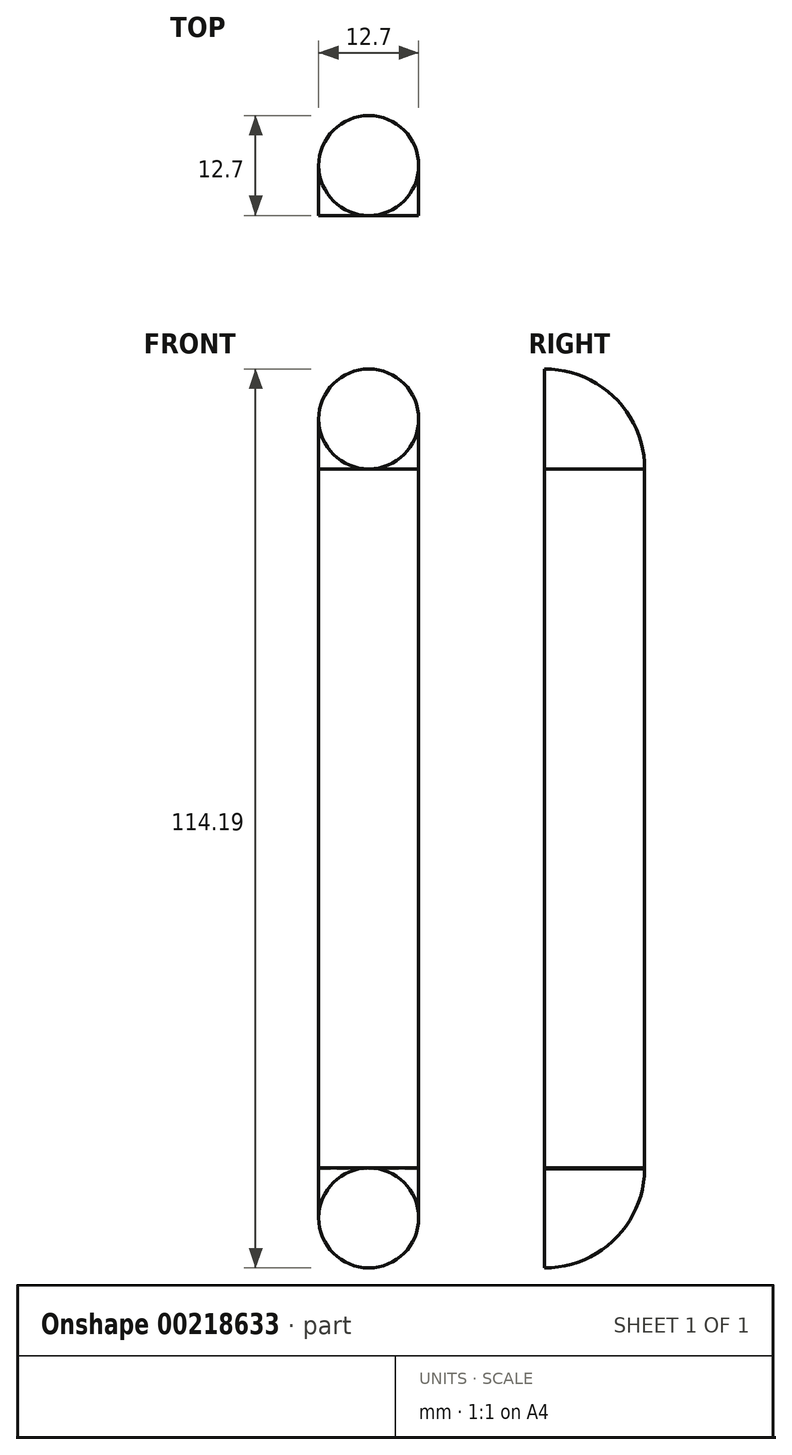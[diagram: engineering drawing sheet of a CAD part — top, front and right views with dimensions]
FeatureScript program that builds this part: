
annotation { "Feature Type Name" : "Feature", "Feature Type Description" : "" }
export const myFeature = defineFeature(function(context is Context, id is Id, definition is map)
    precondition{}
    {
        {
            var Q0;
            Q0=qCreatedBy(makeId("Front.planeOp"),FACE);
            var sketch = newSketch(context, id + "F0", { "sketchPlane" : qUnion([Q0])});
            skCircle(sketch, "E0", {"center": v(0, 53.81) * mm, "radius": 6.35 * mm});
            skCircle(sketch, "E1", {"center": v(0, -47.68) * mm, "radius": 6.35 * mm});
            skLineSegment(sketch, "E2", {"start": v(0, 47.46) * mm, "end": v(51.11, 47.46) * mm});
            skLineSegment(sketch, "E3", {"start": v(0, 47.46) * mm, "end": v(-41.36, 47.46) * mm});
            skLineSegment(sketch, "E4", {"start": v(0, -41.33) * mm, "end": v(50.82, -41.33) * mm});
            skLineSegment(sketch, "E5", {"start": v(0, -41.33) * mm, "end": v(-37.52, -41.33) * mm});
            skSolve(sketch);
        }
        {
            var Q0;
            Q0=makeQuery(id+"F0.imprint","IMPRINT",FACE,{"disambiguationData":[TD([[makeQuery(id+"F0.imprint","IMPRINT",EDGE,{"derivedFrom":sQuery(id+"F0.wireOp",EDGE,"E0")}),1.0]])]});
            var Q1;
            Q1=sQuery(id+"F0.wireOp",EDGE,"E3");
            revolve(context, id + "F1", {"entities" : qUnion([Q0]), "axis" : qUnion([Q1]), "revolveType" : RevolveType.ONE_DIRECTION, "angle" : 90 * degree});
        }
        {
            var Q0;
            Q0=makeQuery(id+"F0.imprint","IMPRINT",FACE,{"disambiguationData":[TD([[makeQuery(id+"F0.imprint","IMPRINT",EDGE,{"derivedFrom":sQuery(id+"F0.wireOp",EDGE,"E1")}),1.0]])]});
            var Q1;
            Q1=sQuery(id+"F0.wireOp",EDGE,"E5");
            revolve(context, id + "F2", {"entities" : qUnion([Q0]), "axis" : qUnion([Q1]), "revolveType" : RevolveType.ONE_DIRECTION, "oppositeDirection" : true, "angle" : 90 * degree});
        }
        {
            var Q0;
            Q0=makeQuery(id+"F1.opRevolve","CAP_FACE",FACE,{"disambiguationData":[OSD([sQuery(id+"F0.wireOp",EDGE,"E0")])],"isStart":false});
            extrude(context, id + "F3", {"entities" : qUnion([Q0]), "depth" : 88.93 * mm});
        }
    });
